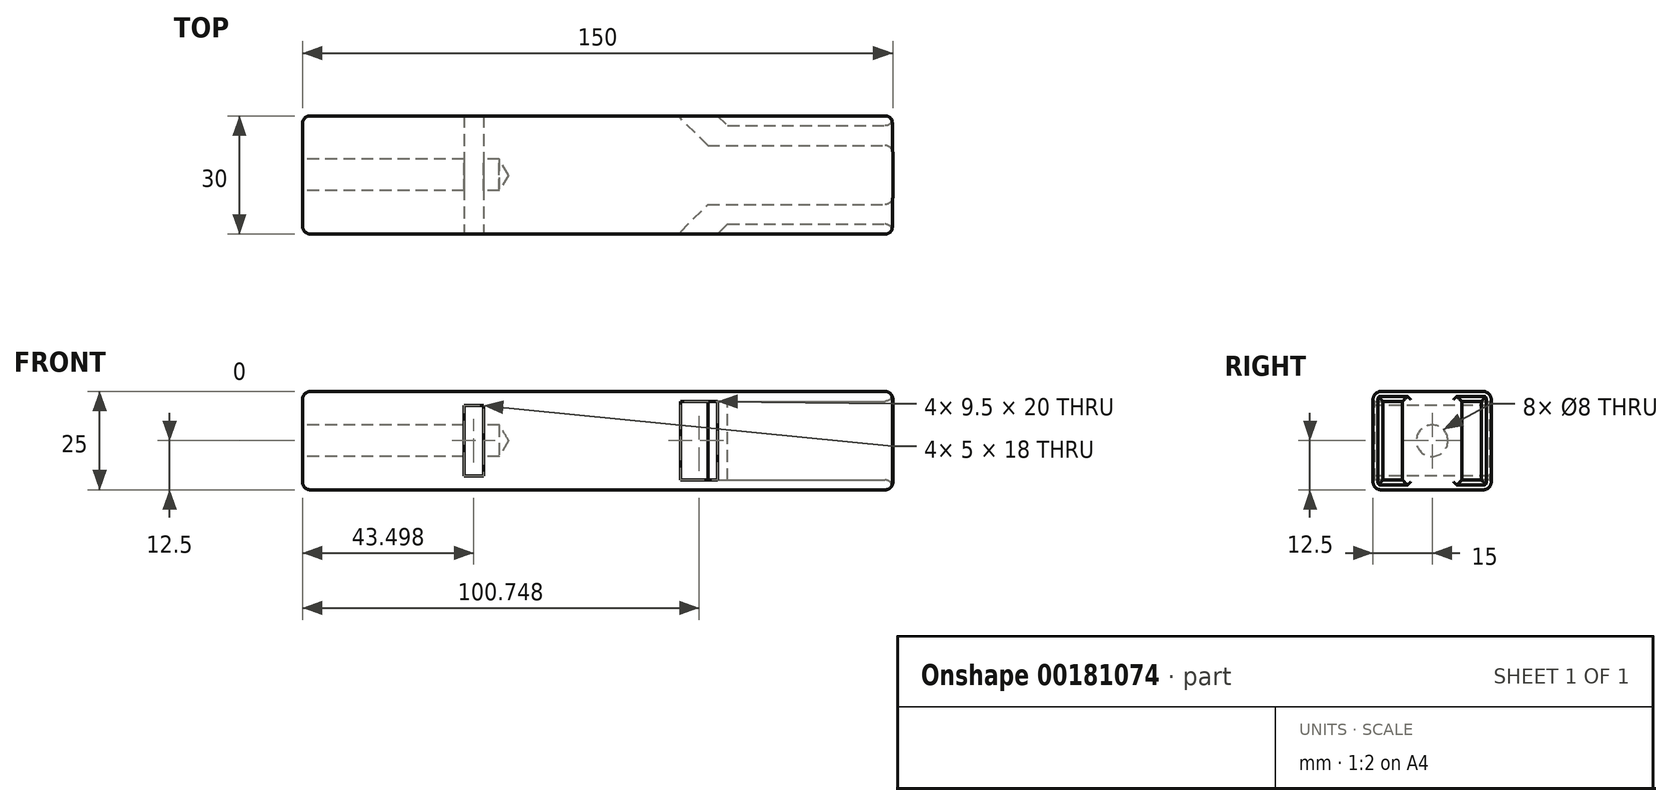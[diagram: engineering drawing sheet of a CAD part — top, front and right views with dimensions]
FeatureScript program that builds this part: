
annotation { "Feature Type Name" : "Feature", "Feature Type Description" : "" }
export const myFeature = defineFeature(function(context is Context, id is Id, definition is map)
    precondition{}
    {
        {
            var Q0;
            Q0=qCreatedBy(makeId("Top.planeOp"),FACE);
            var sketch = newSketch(context, id + "F0", { "sketchPlane" : qUnion([Q0])});
            skLineSegment(sketch, "E0.bottom", {"start": v(-186.5, 24.3) * mm, "end": v(-36.5, 24.3) * mm});
            skLineSegment(sketch, "E0.top", {"start": v(-186.5, -5.7) * mm, "end": v(-36.5, -5.7) * mm});
            skLineSegment(sketch, "E0.left", {"start": v(-186.5, 24.3) * mm, "end": v(-186.5, -5.7) * mm});
            skLineSegment(sketch, "E0.right", {"start": v(-36.5, 24.3) * mm, "end": v(-36.5, -5.7) * mm});
            skSolve(sketch);
        }
        {
            var Q0;
            Q0 = qSketchRegion(id + "F0", true);
            extrude(context, id + "F1", {"entities" : qUnion([Q0]), "depth" : 25 * mm});
        }
        {
            var Q0;
            Q0=makeQuery(id+"F1.opExtrude","SWEPT_FACE",FACE,{"disambiguationData":[OSD([sQuery(id+"F0.wireOp",EDGE,"E0.right")])]});
            var sketch = newSketch(context, id + "F2", { "sketchPlane" : qUnion([Q0])});
            skLineSegment(sketch, "E1.bottom", {"start": v(21.8, 22.5) * mm, "end": v(16.8, 22.5) * mm});
            skLineSegment(sketch, "E1.top", {"start": v(21.8, 2.5) * mm, "end": v(16.8, 2.5) * mm});
            skLineSegment(sketch, "E1.left", {"start": v(21.8, 22.5) * mm, "end": v(21.8, 2.5) * mm});
            skLineSegment(sketch, "E1.right", {"start": v(16.8, 22.5) * mm, "end": v(16.8, 2.5) * mm});
            skLineSegment(sketch, "E2.bottom", {"start": v(-3.2, 22.5) * mm, "end": v(1.8, 22.5) * mm});
            skLineSegment(sketch, "E2.top", {"start": v(-3.2, 2.5) * mm, "end": v(1.8, 2.5) * mm});
            skLineSegment(sketch, "E2.left", {"start": v(-3.2, 22.5) * mm, "end": v(-3.2, 2.5) * mm});
            skLineSegment(sketch, "E2.right", {"start": v(1.8, 22.5) * mm, "end": v(1.8, 2.5) * mm});
            skSolve(sketch);
        }
        {
            var Q0;
            Q0 = qSketchRegion(id + "F2", true);
            extrude(context, id + "F3", {"entities" : qUnion([Q0]), "operationType" : NewBodyOperationType.REMOVE, "oppositeDirection" : true, "depth" : 50 * mm});
        }
        {
            var Q0;
            Q0=makeQuery(id+"F1.opExtrude","SWEPT_FACE",FACE,{"disambiguationData":[OSD([sQuery(id+"F0.wireOp",EDGE,"E0.top")])]});
            var sketch = newSketch(context, id + "F4", { "sketchPlane" : qUnion([Q0])});
            skLineSegment(sketch, "E3.bottom", {"start": v(-90.5, 22.5) * mm, "end": v(-85.5, 22.5) * mm});
            skLineSegment(sketch, "E3.top", {"start": v(-90.5, 2.5) * mm, "end": v(-85.5, 2.5) * mm});
            skLineSegment(sketch, "E3.left", {"start": v(-90.5, 22.5) * mm, "end": v(-90.5, 2.5) * mm});
            skLineSegment(sketch, "E3.right", {"start": v(-85.5, 22.5) * mm, "end": v(-85.5, 2.5) * mm});
            skSolve(sketch);
        }
        {
            var Q0;
            Q0 = qSketchRegion(id + "F4", true);
            extrude(context, id + "F5", {"entities" : qUnion([Q0]), "operationType" : NewBodyOperationType.REMOVE, "oppositeDirection" : true, "depth" : 7.5 * mm});
        }
        {
            var Q0;
            Q0=makeQuery(id+"F5.boolean.opBoolean","COPY",EDGE,{"derivedFrom":makeQuery(id+"F5.opExtrude","CAP_EDGE",EDGE,{"disambiguationData":[OSD([sQuery(id+"F4.wireOp",EDGE,"E3.left")])],"isStart":false})});
            chamfer(context, id + "F6", {"entities" : qUnion([Q0]), "width" : 7 * mm, "tangentPropagation" : true});
        }
        {
            var Q0;
            Q0=makeQuery(id+"F5.boolean.opBoolean","INTERSECT",EDGE,{"derivedFrom":[makeQuery(id+"F3.boolean.opBoolean","COPY",FACE,{"derivedFrom":makeQuery(id+"F3.opExtrude","SWEPT_FACE",FACE,{"disambiguationData":[OSD([sQuery(id+"F2.wireOp",EDGE,"E2.left")])]})}),makeQuery(id+"F5.opExtrude","SWEPT_FACE",FACE,{"disambiguationData":[OSD([sQuery(id+"F4.wireOp",EDGE,"E3.right")])]})]});
            chamfer(context, id + "F7", {"entities" : qUnion([Q0]), "width" : 7 * mm, "tangentPropagation" : true});
        }
        {
            var Q0;
            Q0=makeQuery(id+"F1.opExtrude","SWEPT_FACE",FACE,{"disambiguationData":[OSD([sQuery(id+"F0.wireOp",EDGE,"E0.bottom")])]});
            var sketch = newSketch(context, id + "F8", { "sketchPlane" : qUnion([Q0])});
            skLineSegment(sketch, "E4.bottom", {"start": v(85.5, 22.5) * mm, "end": v(90.5, 22.5) * mm});
            skLineSegment(sketch, "E4.top", {"start": v(85.5, 2.5) * mm, "end": v(90.5, 2.5) * mm});
            skLineSegment(sketch, "E4.left", {"start": v(85.5, 22.5) * mm, "end": v(85.5, 2.5) * mm});
            skLineSegment(sketch, "E4.right", {"start": v(90.5, 22.5) * mm, "end": v(90.5, 2.5) * mm});
            skSolve(sketch);
        }
        {
            var Q0;
            Q0 = qSketchRegion(id + "F8", true);
            extrude(context, id + "F9", {"entities" : qUnion([Q0]), "operationType" : NewBodyOperationType.REMOVE, "oppositeDirection" : true, "depth" : 7.5 * mm});
        }
        {
            var Q0;
            Q0=makeQuery(id+"F9.boolean.opBoolean","COPY",EDGE,{"derivedFrom":makeQuery(id+"F9.opExtrude","CAP_EDGE",EDGE,{"disambiguationData":[OSD([sQuery(id+"F8.wireOp",EDGE,"E4.right")])],"isStart":false})});
            var Q1;
            Q1=makeQuery(id+"F9.boolean.opBoolean","INTERSECT",EDGE,{"derivedFrom":[makeQuery(id+"F3.boolean.opBoolean","COPY",FACE,{"derivedFrom":makeQuery(id+"F3.opExtrude","SWEPT_FACE",FACE,{"disambiguationData":[OSD([sQuery(id+"F2.wireOp",EDGE,"E1.left")])]})}),makeQuery(id+"F9.opExtrude","SWEPT_FACE",FACE,{"disambiguationData":[OSD([sQuery(id+"F8.wireOp",EDGE,"E4.left")])]})]});
            chamfer(context, id + "F10", {"entities" : qUnion([Q0, Q1]), "width" : 7 * mm, "tangentPropagation" : true});
        }
        {
            var Q0;
            Q0=makeQuery(id+"F1.opExtrude","SWEPT_FACE",FACE,{"disambiguationData":[OSD([sQuery(id+"F0.wireOp",EDGE,"E0.right")])]});
            fillet(context, id + "F11", {"entities" : qUnion([Q0]), "radius" : 2 * mm, "tangentPropagation" : true, "allowEdgeOverflow" : false});
        }
        {
            var Q0;
            Q0=makeQuery(id+"F1.opExtrude","CAP_EDGE",EDGE,{"disambiguationData":[OSD([sQuery(id+"F0.wireOp",EDGE,"E0.top")])],"isStart":true});
            var Q1;
            Q1=makeQuery(id+"F1.opExtrude","CAP_EDGE",EDGE,{"disambiguationData":[OSD([sQuery(id+"F0.wireOp",EDGE,"E0.bottom")])],"isStart":true});
            var Q2;
            Q2=makeQuery(id+"F1.opExtrude","CAP_EDGE",EDGE,{"disambiguationData":[OSD([sQuery(id+"F0.wireOp",EDGE,"E0.bottom")])],"isStart":false});
            var Q3;
            Q3=makeQuery(id+"F1.opExtrude","CAP_EDGE",EDGE,{"disambiguationData":[OSD([sQuery(id+"F0.wireOp",EDGE,"E0.top")])],"isStart":false});
            fillet(context, id + "F12", {"entities" : qUnion([Q0, Q1, Q2, Q3]), "radius" : 2 * mm, "tangentPropagation" : true, "allowEdgeOverflow" : false});
        }
        {
            var Q0;
            Q0=makeQuery(id+"F1.opExtrude","SWEPT_FACE",FACE,{"disambiguationData":[OSD([sQuery(id+"F0.wireOp",EDGE,"E0.left")])]});
            fillet(context, id + "F13", {"entities" : qUnion([Q0]), "radius" : 2 * mm, "tangentPropagation" : true, "allowEdgeOverflow" : false});
        }
        {
            var Q0;
            Q0=makeQuery(id+"F1.opExtrude","SWEPT_FACE",FACE,{"disambiguationData":[OSD([sQuery(id+"F0.wireOp",EDGE,"E0.top")])]});
            var sketch = newSketch(context, id + "F14", { "sketchPlane" : qUnion([Q0])});
            skLineSegment(sketch, "E5.bottom", {"start": v(-145.5, 21.5) * mm, "end": v(-140.5, 21.5) * mm});
            skLineSegment(sketch, "E5.top", {"start": v(-145.5, 3.5) * mm, "end": v(-140.5, 3.5) * mm});
            skLineSegment(sketch, "E5.left", {"start": v(-145.5, 21.5) * mm, "end": v(-145.5, 3.5) * mm});
            skLineSegment(sketch, "E5.right", {"start": v(-140.5, 21.5) * mm, "end": v(-140.5, 3.5) * mm});
            skSolve(sketch);
        }
        {
            var Q0;
            Q0 = qSketchRegion(id + "F14", true);
            extrude(context, id + "F15", {"entities" : qUnion([Q0]), "operationType" : NewBodyOperationType.REMOVE, "oppositeDirection" : true, "depth" : 50 * mm});
        }
        {
            var Q0;
            Q0=makeQuery(id+"F1.opExtrude","SWEPT_FACE",FACE,{"disambiguationData":[OSD([sQuery(id+"F0.wireOp",EDGE,"E0.left")])]});
            var sketch = newSketch(context, id + "F16", { "sketchPlane" : qUnion([Q0])});
            skPoint(sketch, "E6", {"position": v(-9.3, 12.5) * mm});
            skPoint(sketch, "E6.positionSnap0", {"position": v(-22.3, 12.5) * mm});
            skPoint(sketch, "E6.positionSnap1", {"position": v(-9.3, 23) * mm});
            skSolve(sketch);
        }
        {
            var Q0;
            Q0=sQuery(id+"F16.wireOp",VERTEX,"E6");
            var Q1;
            Q1=makeQuery(id+"F1.opExtrude","SWEPT_BODY",BODY,{"disambiguationData":[OSD([sQuery(id+"F0.wireOp",EDGE,"E0.bottom"),sQuery(id+"F0.wireOp",EDGE,"E0.top"),sQuery(id+"F0.wireOp",EDGE,"E0.left"),sQuery(id+"F0.wireOp",EDGE,"E0.right")])]});
            hole(context, id + "F17", {"style" : HoleStyle.SIMPLE, "endStyle" : HoleEndStyle.BLIND, "holeDiameter" : 8 * mm, "holeDepth" : 50 * mm, "locations" : qUnion([Q0]), "scope" : qUnion([Q1])});
        }
    });
